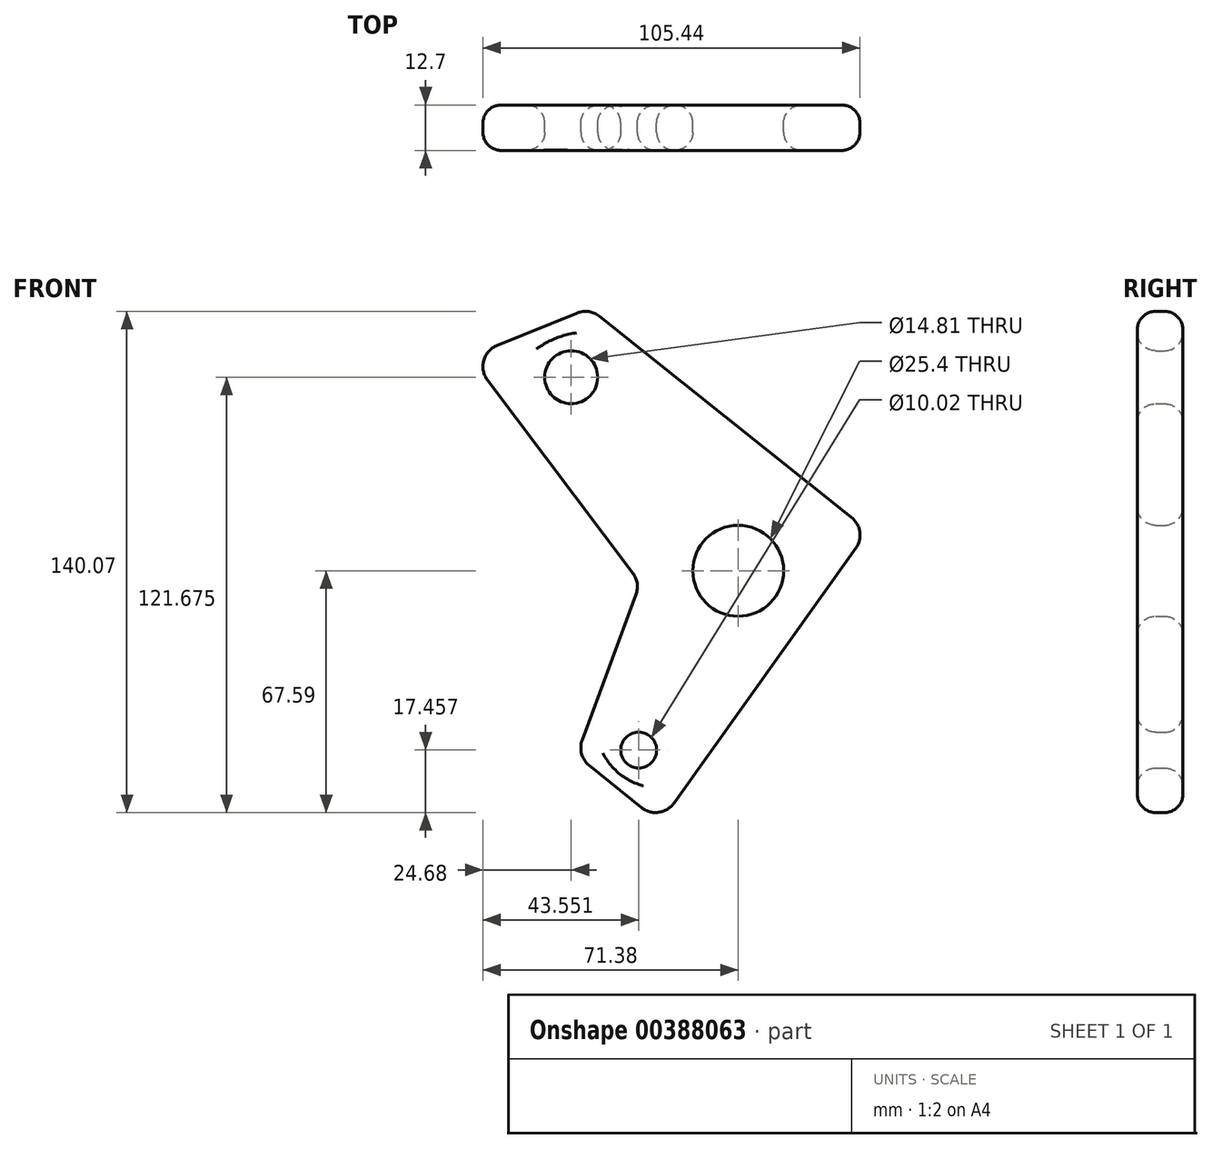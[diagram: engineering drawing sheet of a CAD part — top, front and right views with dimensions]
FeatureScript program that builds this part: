
annotation { "Feature Type Name" : "Feature", "Feature Type Description" : "" }
export const myFeature = defineFeature(function(context is Context, id is Id, definition is map)
    precondition{}
    {
        {
            var Q0;
            Q0=qCreatedBy(makeId("Front.planeOp"),FACE);
            var sketch = newSketch(context, id + "F0", { "sketchPlane" : qUnion([Q0])});
            skCircle(sketch, "E0", {"center": v(0, 0) * mm, "radius": 12.7 * mm});
            skCircle(sketch, "E1", {"center": v(-46.7, 54.08) * mm, "radius": 7.4 * mm});
            skCircle(sketch, "E2", {"center": v(-27.83, -50.13) * mm, "radius": 5.01 * mm});
            skLineSegment(sketch, "E3", {"start": v(-29.47, -0.63) * mm, "end": v(-70.1, 53.26) * mm});
            skLineSegment(sketch, "E4", {"start": v(-38.78, 71.1) * mm, "end": v(31.67, 14.91) * mm});
            skLineSegment(sketch, "E5", {"start": v(32.87, 6.26) * mm, "end": v(-17.95, -64.93) * mm});
            skLineSegment(sketch, "E6", {"start": v(-28.59, -6.65) * mm, "end": v(-43.62, -47.3) * mm});
            skLineSegment(sketch, "E7", {"start": v(-41.65, -54.45) * mm, "end": v(-27.1, -66.19) * mm});
            skLineSegment(sketch, "E8", {"start": v(-45.13, 72.01) * mm, "end": v(-67.42, 62.96) * mm});
            skPoint(sketch, "E9.visualSharp", {"position": v(-41.69, 73.4) * mm});
            skArc(sketch, "E9.filletArc", {"start": v(-38.78, 71.1) * mm, "mid": v(-41.83, 72.41) * mm, "end": v(-45.13, 72.01) * mm});
            skPoint(sketch, "E10.visualSharp", {"position": v(-75.07, 59.86) * mm});
            skArc(sketch, "E10.filletArc", {"start": v(-67.42, 62.96) * mm, "mid": v(-71.15, 58.77) * mm, "end": v(-70.1, 53.26) * mm});
            skPoint(sketch, "E11.visualSharp", {"position": v(-27.38, -3.4) * mm});
            skArc(sketch, "E11.filletArc", {"start": v(-28.59, -6.65) * mm, "mid": v(-28.26, -3.53) * mm, "end": v(-29.47, -0.63) * mm});
            skPoint(sketch, "E12.visualSharp", {"position": v(-45.2, -51.59) * mm});
            skArc(sketch, "E12.filletArc", {"start": v(-43.62, -47.3) * mm, "mid": v(-43.79, -51.2) * mm, "end": v(-41.65, -54.45) * mm});
            skPoint(sketch, "E13.visualSharp", {"position": v(-21.86, -70.41) * mm});
            skArc(sketch, "E13.filletArc", {"start": v(-27.1, -66.19) * mm, "mid": v(-22.25, -67.54) * mm, "end": v(-17.95, -64.93) * mm});
            skPoint(sketch, "E14.visualSharp", {"position": v(36.37, 11.16) * mm});
            skArc(sketch, "E14.filletArc", {"start": v(32.87, 6.26) * mm, "mid": v(34, 10.83) * mm, "end": v(31.67, 14.91) * mm});
            skSolve(sketch);
        }
        {
            var Q0;
            Q0 = qSketchRegion(id + "F0", true);
            extrude(context, id + "F1", {"entities" : qUnion([Q0]), "depth" : 12.7 * mm});
        }
        {
            var Q0;
            Q0=makeQuery(id+"F1.opExtrude","CAP_FACE",FACE,{"disambiguationData":[OSD([sQuery(id+"F0.wireOp",EDGE,"E0"),sQuery(id+"F0.wireOp",EDGE,"E1"),sQuery(id+"F0.wireOp",EDGE,"E2"),sQuery(id+"F0.wireOp",EDGE,"E3"),sQuery(id+"F0.wireOp",EDGE,"E4"),sQuery(id+"F0.wireOp",EDGE,"E5"),sQuery(id+"F0.wireOp",EDGE,"E6"),sQuery(id+"F0.wireOp",EDGE,"E7"),sQuery(id+"F0.wireOp",EDGE,"E8"),sQuery(id+"F0.wireOp",EDGE,"E9.filletArc"),sQuery(id+"F0.wireOp",EDGE,"E10.filletArc"),sQuery(id+"F0.wireOp",EDGE,"E11.filletArc"),sQuery(id+"F0.wireOp",EDGE,"E12.filletArc"),sQuery(id+"F0.wireOp",EDGE,"E13.filletArc"),sQuery(id+"F0.wireOp",EDGE,"E14.filletArc")])],"isStart":false});
            fillet(context, id + "F2", {"entities" : qUnion([Q0]), "radius" : 5.08 * mm, "tangentPropagation" : true, "allowEdgeOverflow" : false});
        }
        {
            var Q0;
            Q0=makeQuery(id+"F1.opExtrude","CAP_FACE",FACE,{"disambiguationData":[OSD([sQuery(id+"F0.wireOp",EDGE,"E0"),sQuery(id+"F0.wireOp",EDGE,"E1"),sQuery(id+"F0.wireOp",EDGE,"E2"),sQuery(id+"F0.wireOp",EDGE,"E3"),sQuery(id+"F0.wireOp",EDGE,"E4"),sQuery(id+"F0.wireOp",EDGE,"E5"),sQuery(id+"F0.wireOp",EDGE,"E6"),sQuery(id+"F0.wireOp",EDGE,"E7"),sQuery(id+"F0.wireOp",EDGE,"E8"),sQuery(id+"F0.wireOp",EDGE,"E9.filletArc"),sQuery(id+"F0.wireOp",EDGE,"E10.filletArc"),sQuery(id+"F0.wireOp",EDGE,"E11.filletArc"),sQuery(id+"F0.wireOp",EDGE,"E12.filletArc"),sQuery(id+"F0.wireOp",EDGE,"E13.filletArc"),sQuery(id+"F0.wireOp",EDGE,"E14.filletArc")])],"isStart":true});
            fillet(context, id + "F3", {"entities" : qUnion([Q0]), "radius" : 5.08 * mm, "tangentPropagation" : true, "allowEdgeOverflow" : false});
        }
    });
